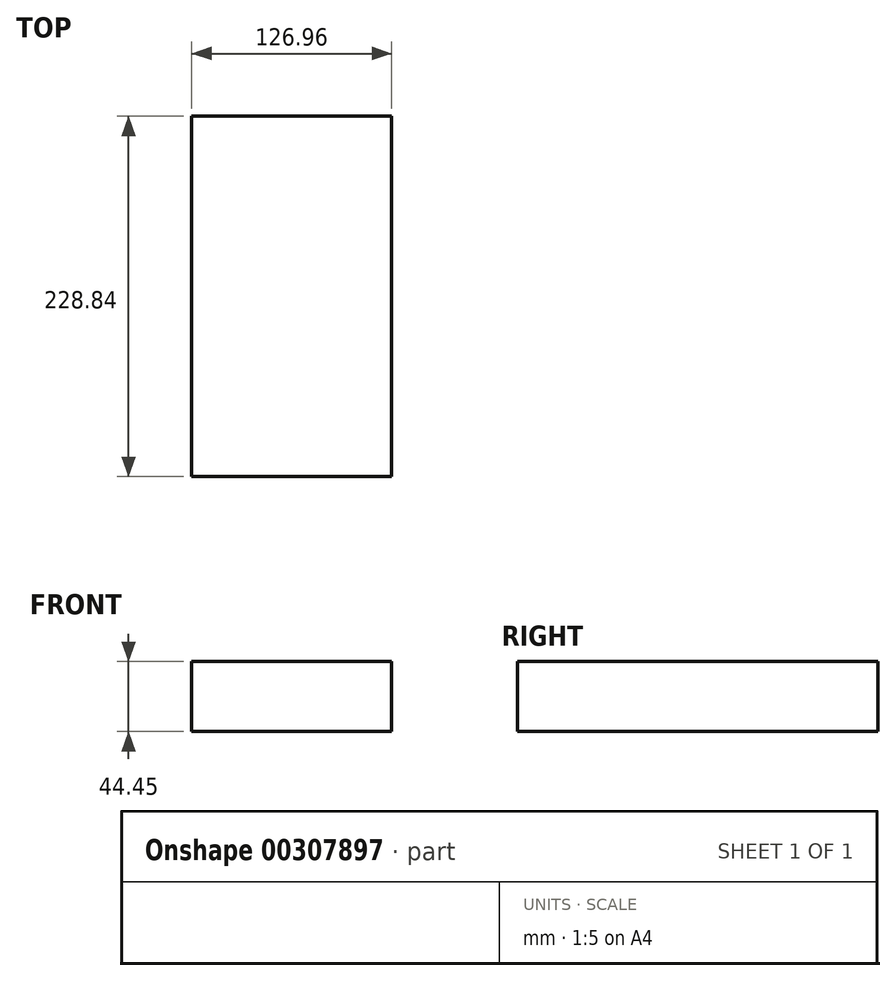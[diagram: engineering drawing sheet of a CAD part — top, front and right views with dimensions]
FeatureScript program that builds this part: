
annotation { "Feature Type Name" : "Feature", "Feature Type Description" : "" }
export const myFeature = defineFeature(function(context is Context, id is Id, definition is map)
    precondition{}
    {
        {
            var Q0;
            Q0=qCreatedBy(makeId("Top.planeOp"),FACE);
            var sketch = newSketch(context, id + "F0", { "sketchPlane" : qUnion([Q0])});
            skLineSegment(sketch, "E0.bottom", {"start": v(-62.5, 54.34) * mm, "end": v(64.46, 54.34) * mm});
            skLineSegment(sketch, "E0.top", {"start": v(-62.5, -174.5) * mm, "end": v(64.46, -174.5) * mm});
            skLineSegment(sketch, "E0.left", {"start": v(-62.5, 54.34) * mm, "end": v(-62.5, -174.5) * mm});
            skLineSegment(sketch, "E0.right", {"start": v(64.46, 54.34) * mm, "end": v(64.46, -174.5) * mm});
            skSolve(sketch);
        }
        {
            var Q0;
            Q0=makeQuery(id+"F0.imprint","IMPRINT",FACE,{"disambiguationData":[TD([[makeQuery(id+"F0.imprint","IMPRINT",EDGE,{"derivedFrom":sQuery(id+"F0.wireOp",EDGE,"E0.bottom")}),-1.0]])]});
            extrude(context, id + "F1", {"entities" : qUnion([Q0]), "depth" : 44.45 * mm});
        }
    });
